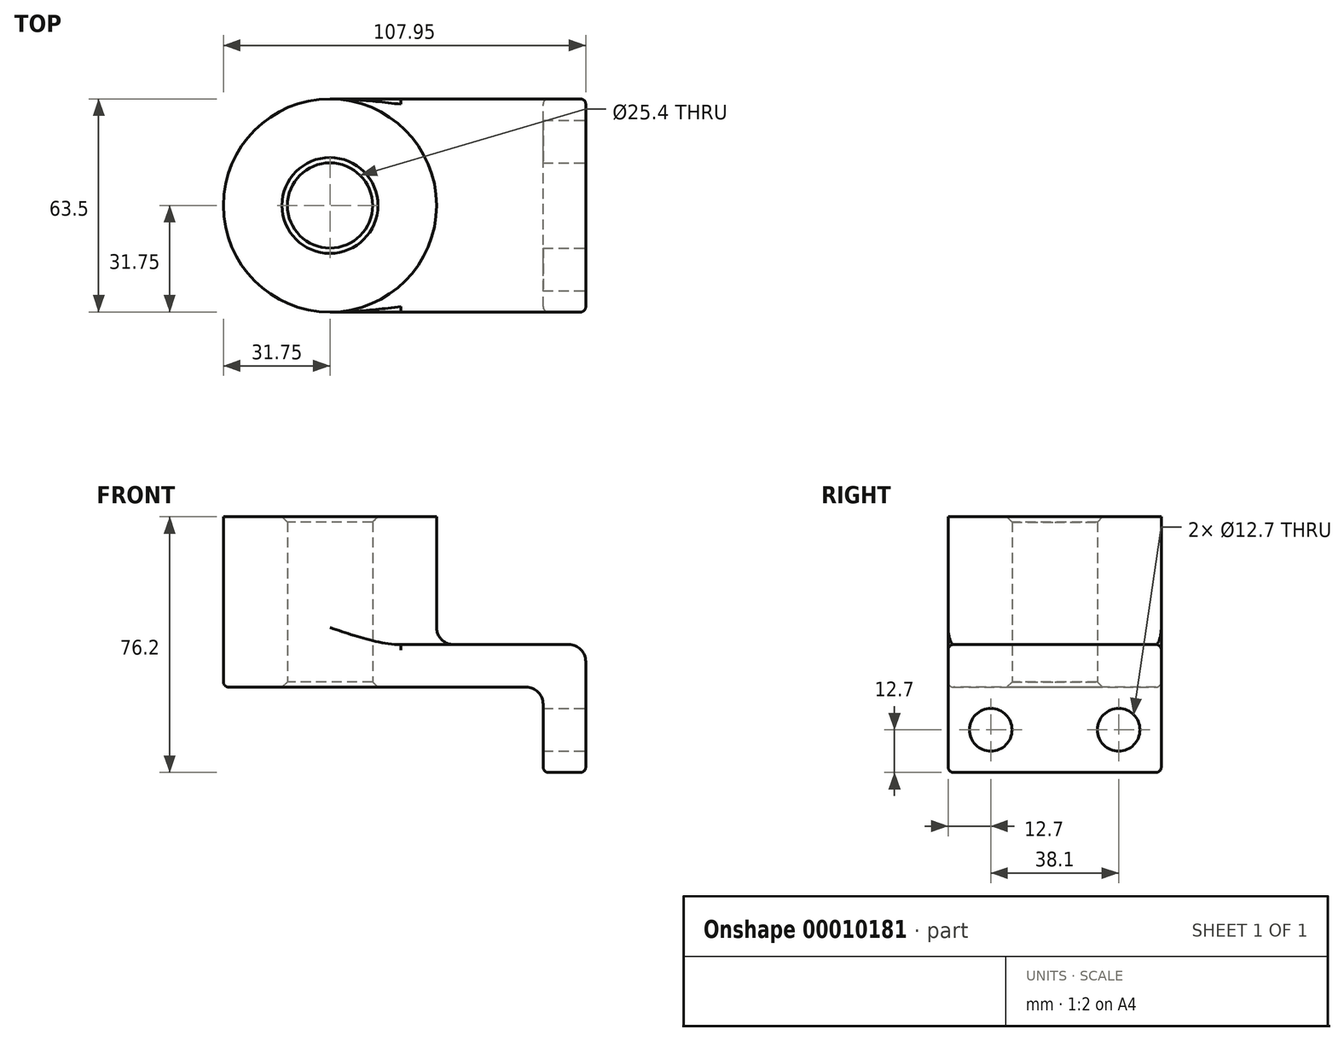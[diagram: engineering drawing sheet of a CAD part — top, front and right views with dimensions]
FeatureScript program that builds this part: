
annotation { "Feature Type Name" : "Feature", "Feature Type Description" : "" }
export const myFeature = defineFeature(function(context is Context, id is Id, definition is map)
    precondition{}
    {
        {
            var Q0;
            Q0=qCreatedBy(makeId("Top.planeOp"),FACE);
            var sketch = newSketch(context, id + "F0", { "sketchPlane" : qUnion([Q0])});
            skLineSegment(sketch, "E0.rect.bottom", {"start": v(-38.1, 31.75) * mm, "end": v(38.1, 31.75) * mm});
            skLineSegment(sketch, "E0.rect.top", {"start": v(-38.1, -31.75) * mm, "end": v(38.1, -31.75) * mm});
            skLineSegment(sketch, "E0.rect.left", {"start": v(-38.1, 31.75) * mm, "end": v(-38.1, -31.75) * mm});
            skLineSegment(sketch, "E0.rect.right", {"start": v(38.1, 31.75) * mm, "end": v(38.1, -31.75) * mm});
            skPoint(sketch, "E0.rect.middle", {"position": v(0, 0) * mm});
            skCircle(sketch, "E1", {"center": v(-38.1, 0) * mm, "radius": 31.75 * mm});
            skCircle(sketch, "E2", {"center": v(-38.1, 0) * mm, "radius": 12.7 * mm});
            skSolve(sketch);
        }
        {
            var Q0;
            Q0 = qSketchRegion(id + "F0", true);
            extrude(context, id + "F1", {"entities" : qUnion([Q0]), "depth" : 12.7 * mm});
        }
        {
            var Q0;
            {var subQ0=sQuery(id+"F0.wireOp",EDGE,"E2");var subQ1=sQuery(id+"F0.wireOp",EDGE,"E0.rect.left");var subQ3=makeQuery(id+"F0.imprint","INTERSECT",VERTEX,{"disambiguationData":[OD(0.0)],"derivedFrom":[subQ1,subQ0]});Q0=makeQuery(id+"F0.imprint","IMPRINT",FACE,{"disambiguationData":[TD([[makeQuery(id+"F0.imprint","IMPRINT",EDGE,{"disambiguationData":[TD([[subQ3,-1.0]])],"derivedFrom":subQ0}),-1.0]])]});}
            var Q1;
            {var subQ0=sQuery(id+"F0.wireOp",EDGE,"E2");var subQ1=sQuery(id+"F0.wireOp",EDGE,"E0.rect.left");var subQ3=makeQuery(id+"F0.imprint","INTERSECT",VERTEX,{"disambiguationData":[OD(0.0)],"derivedFrom":[subQ1,subQ0]});Q1=makeQuery(id+"F0.imprint","IMPRINT",FACE,{"disambiguationData":[TD([[makeQuery(id+"F0.imprint","IMPRINT",EDGE,{"disambiguationData":[TD([[subQ3,1.0]])],"derivedFrom":subQ0}),-1.0]])]});}
            extrude(context, id + "F2", {"entities" : qUnion([Q0, Q1]), "operationType" : NewBodyOperationType.ADD, "depth" : 50.8 * mm});
        }
        {
            var Q0;
            Q0=makeQuery(id+"F1.opExtrude","SWEPT_FACE",FACE,{"disambiguationData":[OSD([sQuery(id+"F0.wireOp",EDGE,"E0.rect.right")])]});
            var sketch = newSketch(context, id + "F3", { "sketchPlane" : qUnion([Q0])});
            skLineSegment(sketch, "E3.bottom", {"start": v(-31.75, 12.7) * mm, "end": v(31.75, 12.7) * mm});
            skLineSegment(sketch, "E3.top", {"start": v(-31.75, -25.4) * mm, "end": v(31.75, -25.4) * mm});
            skLineSegment(sketch, "E3.left", {"start": v(-31.75, 12.7) * mm, "end": v(-31.75, -25.4) * mm});
            skLineSegment(sketch, "E3.right", {"start": v(31.75, 12.7) * mm, "end": v(31.75, -25.4) * mm});
            skCircle(sketch, "E4", {"center": v(-19.05, -12.7) * mm, "radius": 6.35 * mm});
            skLineSegment(sketch, "E5", {"start": v(0, 0) * mm, "end": v(0, -25.4) * mm, "construction": true});
            skCircle(sketch, "E6.0.MirrorC", {"center": v(19.05, -12.7) * mm, "radius": 6.35 * mm});
            skSolve(sketch);
        }
        {
            var Q0;
            Q0 = qSketchRegion(id + "F3", true);
            extrude(context, id + "F4", {"entities" : qUnion([Q0]), "operationType" : NewBodyOperationType.ADD, "oppositeDirection" : true, "depth" : 12.7 * mm});
        }
        {
            var Q0;
            {var subQ0=sQuery(id+"F0.wireOp",EDGE,"E1");Q0=makeQuery(id+"F2.boolean.opBoolean","INTERSECT",EDGE,{"derivedFrom":[makeQuery(id+"F1.opExtrude","CAP_FACE",FACE,{"disambiguationData":[OSD([sQuery(id+"F0.wireOp",EDGE,"E0.rect.bottom"),sQuery(id+"F0.wireOp",EDGE,"E0.rect.top"),sQuery(id+"F0.wireOp",EDGE,"E0.rect.right"),subQ0,sQuery(id+"F0.wireOp",EDGE,"E2")])],"isStart":false}),makeQuery(id+"F2.opExtrude","SWEPT_FACE",FACE,{"disambiguationData":[OSD([subQ0])]})]});}
            var Q1;
            Q1=makeQuery(id+"F1.opExtrude","CAP_EDGE",EDGE,{"disambiguationData":[OSD([sQuery(id+"F0.wireOp",EDGE,"E0.rect.right")])],"isStart":false});
            var Q2;
            Q2=makeQuery(id+"F4.boolean.opBoolean","INTERSECT",EDGE,{"derivedFrom":[makeQuery(id+"F1.opExtrude","CAP_FACE",FACE,{"disambiguationData":[OSD([sQuery(id+"F0.wireOp",EDGE,"E0.rect.bottom"),sQuery(id+"F0.wireOp",EDGE,"E0.rect.top"),sQuery(id+"F0.wireOp",EDGE,"E0.rect.right"),sQuery(id+"F0.wireOp",EDGE,"E1"),sQuery(id+"F0.wireOp",EDGE,"E2")])],"isStart":true}),makeQuery(id+"F4.opExtrude","CAP_FACE",FACE,{"disambiguationData":[OSD([sQuery(id+"F3.wireOp",EDGE,"E3.bottom"),sQuery(id+"F3.wireOp",EDGE,"E3.top"),sQuery(id+"F3.wireOp",EDGE,"E3.left"),sQuery(id+"F3.wireOp",EDGE,"E3.right"),sQuery(id+"F3.wireOp",EDGE,"E4"),sQuery(id+"F3.wireOp",EDGE,"E6.0.MirrorC")])],"isStart":false})]});
            fillet(context, id + "F5", {"entities" : qUnion([Q0, Q1, Q2]), "radius" : 5.08 * mm, "tangentPropagation" : true, "allowEdgeOverflow" : false});
        }
        {
            var Q0;
            Q0=makeQuery(id+"F1.opExtrude","CAP_EDGE",EDGE,{"disambiguationData":[OSD([sQuery(id+"F0.wireOp",EDGE,"E0.rect.top")])],"isStart":false});
            var Q1;
            Q1=makeQuery(id+"F1.opExtrude","CAP_EDGE",EDGE,{"disambiguationData":[OSD([sQuery(id+"F0.wireOp",EDGE,"E0.rect.top")])],"isStart":true});
            var Q2;
            Q2=makeQuery(id+"F4.opExtrude","CAP_EDGE",EDGE,{"disambiguationData":[OSD([sQuery(id+"F3.wireOp",EDGE,"E3.left")])],"isStart":false});
            var Q3;
            Q3=makeQuery(id+"F4.boolean.opBoolean","MERGE",EDGE,{"derivedFrom":[makeQuery(id+"F1.opExtrude","SWEPT_EDGE",EDGE,{"disambiguationData":[OSD([sQuery(id+"F0.wireOp",EDGE,"E0.rect.top"),sQuery(id+"F0.wireOp",EDGE,"E0.rect.right")])]}),makeQuery(id+"F4.opExtrude","CAP_EDGE",EDGE,{"disambiguationData":[OSD([sQuery(id+"F3.wireOp",EDGE,"E3.left")])],"isStart":true})]});
            var Q4;
            Q4=makeQuery(id+"F4.opExtrude","CAP_EDGE",EDGE,{"disambiguationData":[OSD([sQuery(id+"F3.wireOp",EDGE,"E3.top")])],"isStart":true});
            var Q5;
            Q5=makeQuery(id+"F4.opExtrude","SWEPT_EDGE",EDGE,{"disambiguationData":[OSD([sQuery(id+"F3.wireOp",EDGE,"E3.top"),sQuery(id+"F3.wireOp",EDGE,"E3.left")])]});
            var Q6;
            Q6=makeQuery(id+"F4.opExtrude","SWEPT_EDGE",EDGE,{"disambiguationData":[OSD([sQuery(id+"F3.wireOp",EDGE,"E3.top"),sQuery(id+"F3.wireOp",EDGE,"E3.right")])]});
            var Q7;
            Q7=makeQuery(id+"F4.boolean.opBoolean","MERGE",EDGE,{"derivedFrom":[makeQuery(id+"F1.opExtrude","SWEPT_EDGE",EDGE,{"disambiguationData":[OSD([sQuery(id+"F0.wireOp",EDGE,"E0.rect.bottom"),sQuery(id+"F0.wireOp",EDGE,"E0.rect.right")])]}),makeQuery(id+"F4.opExtrude","CAP_EDGE",EDGE,{"disambiguationData":[OSD([sQuery(id+"F3.wireOp",EDGE,"E3.right")])],"isStart":true})]});
            var Q8;
            Q8=makeQuery(id+"F4.opExtrude","CAP_EDGE",EDGE,{"disambiguationData":[OSD([sQuery(id+"F3.wireOp",EDGE,"E3.right")])],"isStart":false});
            var Q9;
            Q9=makeQuery(id+"F4.opExtrude","CAP_EDGE",EDGE,{"disambiguationData":[OSD([sQuery(id+"F3.wireOp",EDGE,"E3.top")])],"isStart":false});
            var Q10;
            Q10=makeQuery(id+"F1.opExtrude","CAP_EDGE",EDGE,{"disambiguationData":[OSD([sQuery(id+"F0.wireOp",EDGE,"E0.rect.bottom")])],"isStart":false});
            fillet(context, id + "F6", {"entities" : qUnion([Q0, Q1, Q2, Q3, Q4, Q5, Q6, Q7, Q8, Q9, Q10]), "radius" : 1.59 * mm, "tangentPropagation" : true, "allowEdgeOverflow" : false});
        }
        {
            var Q0;
            {var subQ0=sQuery(id+"F0.wireOp",EDGE,"E2");Q0=makeQuery(id+"F2.boolean.opBoolean","MERGE",FACE,{"derivedFrom":[makeQuery(id+"F1.opExtrude","SWEPT_FACE",FACE,{"disambiguationData":[OSD([subQ0])]}),makeQuery(id+"F2.opExtrude","SWEPT_FACE",FACE,{"disambiguationData":[OSD([subQ0])]})]});}
            chamfer(context, id + "F7", {"entities" : qUnion([Q0]), "width" : 1.59 * mm, "tangentPropagation" : true});
        }
    });
